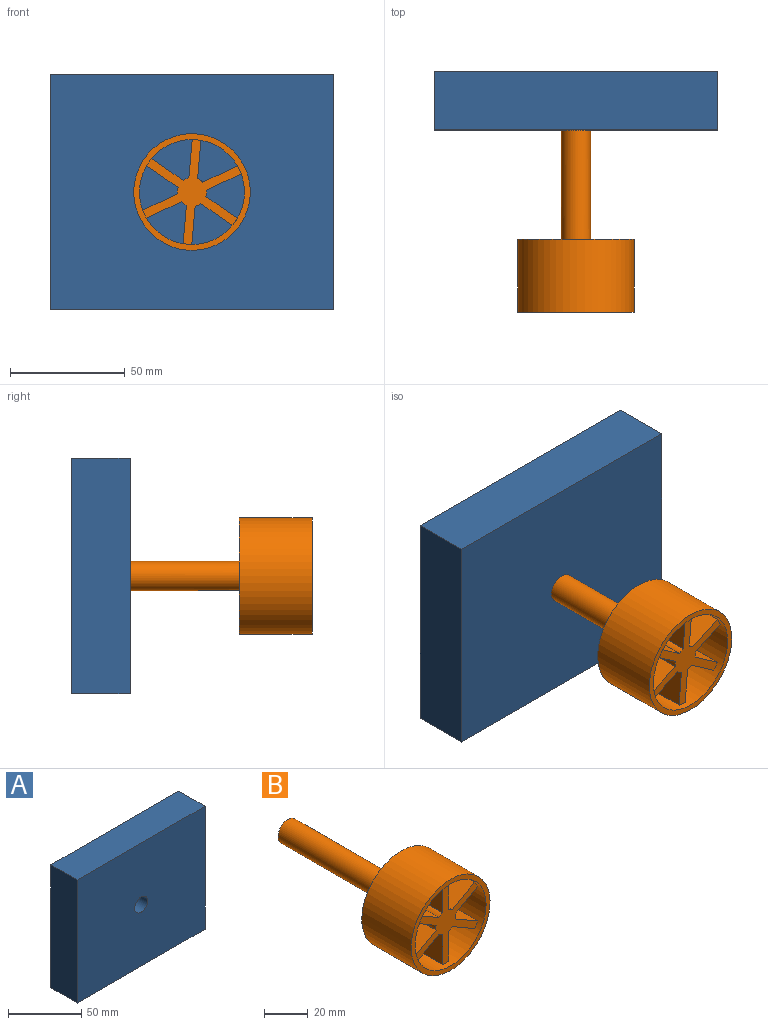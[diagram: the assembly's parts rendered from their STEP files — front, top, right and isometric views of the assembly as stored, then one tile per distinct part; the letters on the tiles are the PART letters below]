
ASSEMBLY  parts=2 mates=1
PART A: 7 faces, bbox 123.4x25.4x102.8 mm
  f0: plane 123.38x25.4mm, normal (0,0,1), area 3133.8mm2, adj f1,f4,f5,f6
  f1: plane 102.77x25.4mm, normal (1,0,0), area 2610.3mm2, adj f0,f2,f5,f6
  f2: plane 123.38x25.4mm, normal (0,0,-1), area 3133.8mm2, adj f1,f4,f5,f6
  f3: cylinder r=6.35mm len=25.4mm, axis (0,-1,0), area 1013.4mm2, adj f5,f6
  f4: plane 102.77x25.4mm, normal (-1,0,0), area 2610.3mm2, adj f0,f2,f5,f6
  f5: plane 123.38x102.77mm, normal (0,1,0), area 12552.7mm2, adj f0,f1,f2,f3,f4
  f6: plane 123.38x102.77mm, normal (0,-1,0), area 12552.7mm2, adj f0,f1,f2,f3,f4
PART B: 25 faces, bbox 50.8x104.8x50.8 mm
  f0: cylinder r=22.86mm len=45.72mm, axis (0,1,0), area 3979mm2, adj f2,f3,f4,f5,f6,f7,f8,f9
  f1: cylinder r=25.4mm len=50.8mm, axis (0,1,0), area 5067.1mm2, adj f2,f3
  f2: plane 50.8x50.8mm, normal (0,-1,0), area 385.1mm2, adj f0,f1
  f3: plane 50.8x50.8mm, normal (0,1,0), area 385.1mm2, adj f0,f1
  f4: plane 25.4x14.48mm, normal (-0.5,0,-0.87), area 424.8mm2, adj f0,f6,f7,f23
  f5: plane 25.4x14.48mm, normal (0.5,0,0.87), area 424.8mm2, adj f0,f6,f7,f23
  f6: plane 45.72x41.36mm, normal (0,-1,0), area 505.7mm2, adj f0,f4,f5,f8,f9,f11,f12,f14
  f7: plane 16.39x11.66mm, normal (0,1,0), area 63.2mm2, adj f0,f4,f5,f23
  f8: plane 25.4x14.48mm, normal (-0.5,0,0.87), area 424.8mm2, adj f0,f6,f10,f23
  f9: plane 25.4x14.48mm, normal (0.5,0,-0.87), area 424.8mm2, adj f0,f6,f10,f23
  f10: plane 16.39x11.66mm, normal (0,1,0), area 63.2mm2, adj f0,f8,f9,f23
  f11: plane 25.4x16.72mm, normal (-1,0,0), area 424.8mm2, adj f0,f6,f13,f23
  f12: plane 25.4x16.72mm, normal (1,0,0), area 424.8mm2, adj f0,f6,f13,f23
  f13: plane 16.8x3.81mm, normal (0,1,0), area 63.2mm2, adj f0,f11,f12,f23
  f14: plane 25.4x14.48mm, normal (-0.5,0,-0.87), area 424.8mm2, adj f0,f6,f16,f23
  f15: plane 25.4x14.48mm, normal (0.5,0,0.87), area 424.8mm2, adj f0,f6,f16,f23
  f16: plane 16.39x11.66mm, normal (0,1,0), area 63.2mm2, adj f0,f14,f15,f23
  f17: plane 25.4x14.48mm, normal (0.5,0,-0.87), area 424.8mm2, adj f0,f6,f19,f23
  f18: plane 25.4x14.48mm, normal (-0.5,0,0.87), area 424.8mm2, adj f0,f6,f19,f23
  f19: plane 16.39x11.66mm, normal (0,1,0), area 63.2mm2, adj f0,f17,f18,f23
  f20: plane 25.4x16.72mm, normal (-1,0,0), area 424.8mm2, adj f0,f6,f22,f23
  f21: plane 25.4x16.72mm, normal (1,0,0), area 424.8mm2, adj f0,f6,f22,f23
  f22: plane 16.8x3.81mm, normal (0,1,0), area 63.2mm2, adj f0,f20,f21,f23
  f23: cylinder r=6.35mm len=101.6mm, axis (0,-1,0), area 3463.9mm2, adj f4,f5,f6,f7,f8,f9,f10,f11
  f24: plane 12.7x12.7mm, normal (0,1,0), area 126.7mm2, adj f23
PLACE A t=(-33.3,8.02,-15.72)mm fixed
PLACE B rot(axis=(0,-1,0),115deg) t=(-33.3,33.42,-15.72)mm
MATE revolute B.f23 <-> A.f3  axis (0,1,0) through (-33.3,122.32,-15.72)mm
